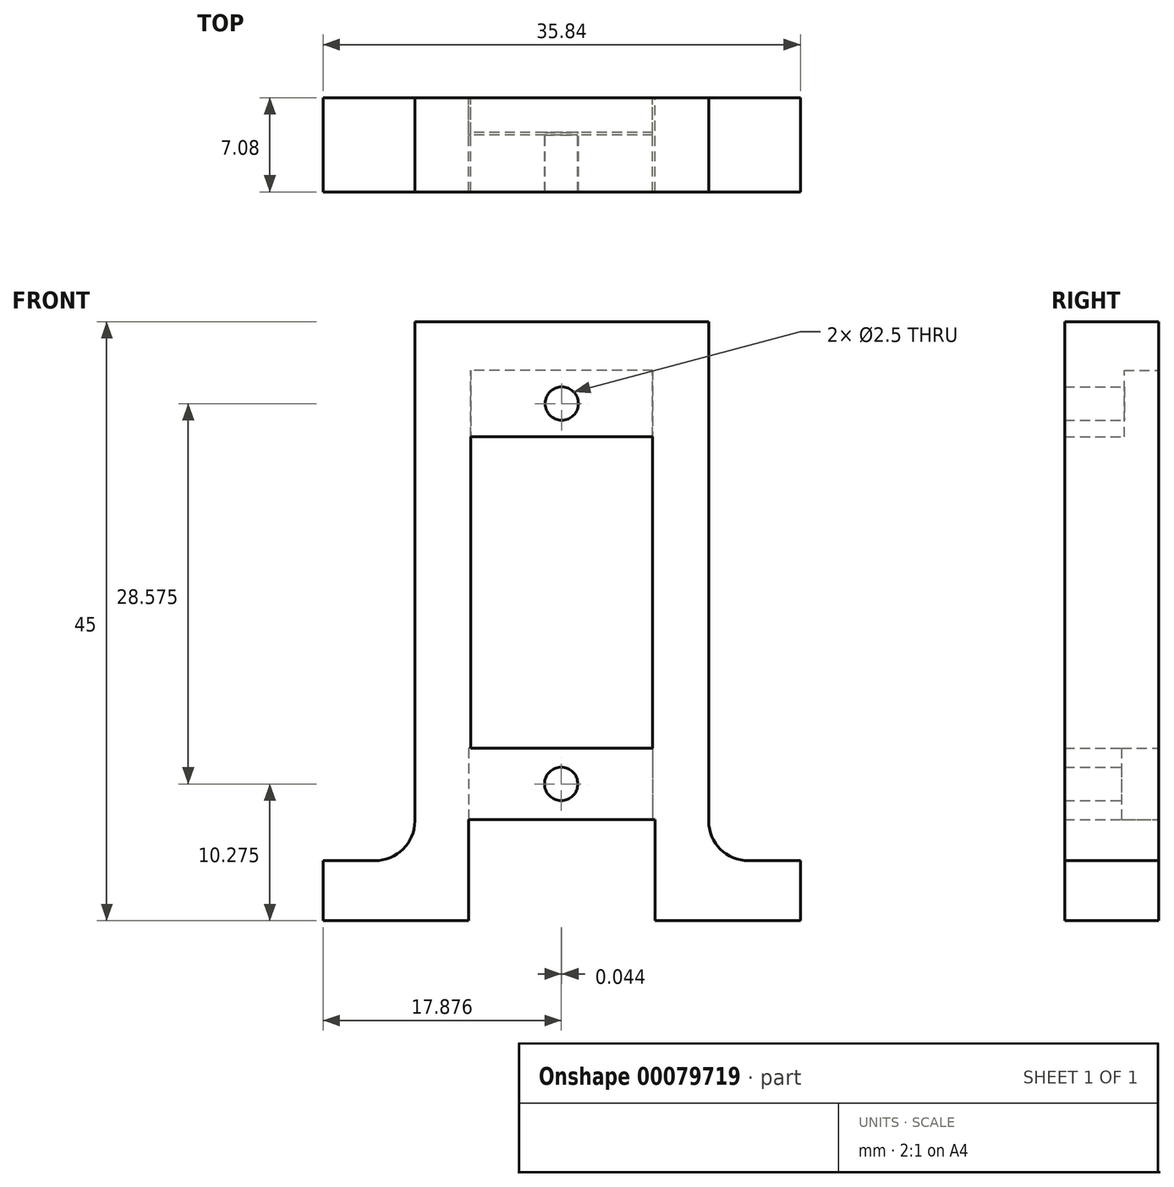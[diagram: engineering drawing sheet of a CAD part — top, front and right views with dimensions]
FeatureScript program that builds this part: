
annotation { "Feature Type Name" : "Feature", "Feature Type Description" : "" }
export const myFeature = defineFeature(function(context is Context, id is Id, definition is map)
    precondition{}
    {
        {
            var Q0;
            Q0=qCreatedBy(makeId("Top.planeOp"),FACE);
            var sketch = newSketch(context, id + "F0", { "sketchPlane" : qUnion([Q0])});
            skLineSegment(sketch, "E0.bottom", {"start": v(17.92, 3.53) * mm, "end": v(-17.92, 3.53) * mm});
            skLineSegment(sketch, "E0.top", {"start": v(17.92, -3.54) * mm, "end": v(-17.92, -3.54) * mm});
            skLineSegment(sketch, "E0.left", {"start": v(17.92, 3.53) * mm, "end": v(17.92, -3.54) * mm});
            skLineSegment(sketch, "E0.right", {"start": v(-17.92, 3.53) * mm, "end": v(-17.92, -3.54) * mm});
            skPoint(sketch, "E0.middle", {"position": v(0, 0) * mm});
            skSolve(sketch);
        }
        {
            var Q0;
            Q0 = qSketchRegion(id + "F0", true);
            extrude(context, id + "F1", {"entities" : qUnion([Q0]), "depth" : 45 * mm});
        }
        {
            var Q0;
            Q0=makeQuery(id+"F1.opExtrude","CAP_FACE",FACE,{"disambiguationData":[OSD([sQuery(id+"F0.wireOp",EDGE,"E0.bottom"),sQuery(id+"F0.wireOp",EDGE,"E0.top"),sQuery(id+"F0.wireOp",EDGE,"E0.left"),sQuery(id+"F0.wireOp",EDGE,"E0.right")])],"isStart":true});
            var sketch = newSketch(context, id + "F2", { "sketchPlane" : qUnion([Q0])});
            skLineSegment(sketch, "E1.bottom", {"start": v(7, 3.54) * mm, "end": v(-7, 3.54) * mm});
            skLineSegment(sketch, "E1.top", {"start": v(7, -3.54) * mm, "end": v(-7, -3.54) * mm});
            skLineSegment(sketch, "E1.left", {"start": v(7, 3.54) * mm, "end": v(7, -3.54) * mm});
            skLineSegment(sketch, "E1.right", {"start": v(-7, 3.54) * mm, "end": v(-7, -3.54) * mm});
            skPoint(sketch, "E1.middle", {"position": v(0, 0) * mm});
            skSolve(sketch);
        }
        {
            var Q0;
            Q0=makeQuery(id+"F1.opExtrude","SWEPT_FACE",FACE,{"disambiguationData":[OSD([sQuery(id+"F0.wireOp",EDGE,"E0.top")])]});
            var sketch = newSketch(context, id + "F3", { "sketchPlane" : qUnion([Q0])});
            skLineSegment(sketch, "E2.bottom", {"start": v(-11.03, 45) * mm, "end": v(11.03, 45) * mm});
            skLineSegment(sketch, "E2.top", {"start": v(-11.03, 0) * mm, "end": v(11.03, 0) * mm});
            skLineSegment(sketch, "E2.left", {"start": v(-11.03, 45) * mm, "end": v(-11.03, 0) * mm});
            skLineSegment(sketch, "E2.right", {"start": v(11.03, 45) * mm, "end": v(11.03, 0) * mm});
            skSolve(sketch);
        }
        {
            var Q0;
            {var subQ0=sQuery(id+"F3.wireOp",EDGE,"E2.right");Q0=makeQuery(id+"F3.imprint","IMPRINT",FACE,{"disambiguationData":[TD([[makeQuery(id+"F3.imprint","IMPRINT",EDGE,{"derivedFrom":subQ0}),1.0]])]});}
            var sketch = newSketch(context, id + "F4", { "sketchPlane" : qUnion([Q0])});
            skLineSegment(sketch, "E3.bottom", {"start": v(11.03, 45) * mm, "end": v(17.92, 45) * mm});
            skLineSegment(sketch, "E3.top", {"start": v(11.03, 4.5) * mm, "end": v(17.92, 4.5) * mm});
            skLineSegment(sketch, "E3.left", {"start": v(11.03, 45) * mm, "end": v(11.03, 4.5) * mm});
            skLineSegment(sketch, "E3.right", {"start": v(17.92, 45) * mm, "end": v(17.92, 4.5) * mm});
            skSolve(sketch);
        }
        {
            var Q0;
            Q0 = qSketchRegion(id + "F4", true);
            var Q1;
            Q1=makeQuery(id+"F1.opExtrude","SWEPT_FACE",FACE,{"disambiguationData":[OSD([sQuery(id+"F0.wireOp",EDGE,"E0.bottom")])]});
            extrude(context, id + "F5", {"entities" : qUnion([Q0]), "operationType" : NewBodyOperationType.REMOVE, "endBound" : BoundingType.UP_TO_SURFACE, "oppositeDirection" : true, "endBoundEntityFace" : qUnion([Q1]), "depth" : 25 * mm});
        }
        {
            var Q0;
            {var subQ0=sQuery(id+"F3.wireOp",EDGE,"E2.left");Q0=makeQuery(id+"F3.imprint","IMPRINT",FACE,{"disambiguationData":[TD([[makeQuery(id+"F3.imprint","IMPRINT",EDGE,{"derivedFrom":subQ0}),-1.0]])]});}
            var sketch = newSketch(context, id + "F6", { "sketchPlane" : qUnion([Q0])});
            skLineSegment(sketch, "E4.bottom", {"start": v(-17.92, 45) * mm, "end": v(-11.03, 45) * mm});
            skLineSegment(sketch, "E4.top", {"start": v(-17.92, 4.5) * mm, "end": v(-11.03, 4.5) * mm});
            skLineSegment(sketch, "E4.left", {"start": v(-17.92, 45) * mm, "end": v(-17.92, 4.5) * mm});
            skLineSegment(sketch, "E4.right", {"start": v(-11.03, 45) * mm, "end": v(-11.03, 4.5) * mm});
            skSolve(sketch);
        }
        {
            var Q0;
            Q0 = qSketchRegion(id + "F6", true);
            var Q1;
            Q1=makeQuery(id+"F1.opExtrude","SWEPT_FACE",FACE,{"disambiguationData":[OSD([sQuery(id+"F0.wireOp",EDGE,"E0.bottom")])]});
            extrude(context, id + "F7", {"entities" : qUnion([Q0]), "operationType" : NewBodyOperationType.REMOVE, "endBound" : BoundingType.UP_TO_SURFACE, "oppositeDirection" : true, "endBoundEntityFace" : qUnion([Q1]), "depth" : 25 * mm});
        }
        {
            var Q0;
            Q0=makeQuery(id+"F1.opExtrude","SWEPT_FACE",FACE,{"disambiguationData":[OSD([sQuery(id+"F0.wireOp",EDGE,"E0.bottom")])]});
            var sketch = newSketch(context, id + "F8", { "sketchPlane" : qUnion([Q0])});
            skSolve(sketch);
        }
        {
            var Q0;
            Q0=makeQuery(id+"F2.imprint","IMPRINT",FACE,{"disambiguationData":[TD([[makeQuery(id+"F2.imprint","IMPRINT",EDGE,{"derivedFrom":sQuery(id+"F2.wireOp",EDGE,"E1.bottom")}),1.0]])]});
            extrude(context, id + "F9", {"entities" : qUnion([Q0]), "operationType" : NewBodyOperationType.REMOVE, "oppositeDirection" : true, "depth" : 7.6 * mm});
        }
        {
            var Q0;
            {var subQ0=sQuery(id+"F0.wireOp",EDGE,"E0.bottom");Q0=makeQuery(id+"F8.imprint","IMPRINT",FACE,{"disambiguationData":[TD([[makeQuery(id+"F8.imprint","IMPRINT",EDGE,{"derivedFrom":makeQuery(id+"F1.opExtrude","CAP_EDGE",EDGE,{"disambiguationData":[OSD([subQ0])],"isStart":true})}),1.0]])]});}
            var sketch = newSketch(context, id + "F10", { "sketchPlane" : qUnion([Q0])});
            skLineSegment(sketch, "E5.bottom", {"start": v(-6.82, 36.35) * mm, "end": v(6.83, 36.35) * mm});
            skLineSegment(sketch, "E5.top", {"start": v(-6.82, 12.95) * mm, "end": v(6.83, 12.95) * mm});
            skLineSegment(sketch, "E5.left", {"start": v(-6.82, 36.35) * mm, "end": v(-6.82, 12.95) * mm});
            skLineSegment(sketch, "E5.right", {"start": v(6.83, 36.35) * mm, "end": v(6.83, 12.95) * mm});
            skSolve(sketch);
        }
        {
            var Q0;
            Q0 = qSketchRegion(id + "F10", true);
            var Q1;
            Q1=makeQuery(id+"F1.opExtrude","SWEPT_FACE",FACE,{"disambiguationData":[OSD([sQuery(id+"F0.wireOp",EDGE,"E0.top")])]});
            extrude(context, id + "F11", {"entities" : qUnion([Q0]), "operationType" : NewBodyOperationType.REMOVE, "endBound" : BoundingType.UP_TO_SURFACE, "oppositeDirection" : true, "endBoundEntityFace" : qUnion([Q1]), "depth" : 25 * mm});
        }
        {
            var Q0;
            Q0=makeQuery(id+"F1.opExtrude","SWEPT_FACE",FACE,{"disambiguationData":[OSD([sQuery(id+"F0.wireOp",EDGE,"E0.bottom")])]});
            var sketch = newSketch(context, id + "F12", { "sketchPlane" : qUnion([Q0])});
            skLineSegment(sketch, "E6.bottom", {"start": v(-6.82, 36.35) * mm, "end": v(6.83, 36.35) * mm});
            skLineSegment(sketch, "E6.top", {"start": v(-6.82, 41.35) * mm, "end": v(6.83, 41.35) * mm});
            skLineSegment(sketch, "E6.left", {"start": v(-6.82, 36.35) * mm, "end": v(-6.82, 41.35) * mm});
            skLineSegment(sketch, "E6.right", {"start": v(6.83, 36.35) * mm, "end": v(6.83, 41.35) * mm});
            skLineSegment(sketch, "E7.bottom", {"start": v(6.83, 36.35) * mm, "end": v(6.83, 36.35) * mm});
            skLineSegment(sketch, "E7.top", {"start": v(6.83, 36.35) * mm, "end": v(6.83, 36.35) * mm});
            skLineSegment(sketch, "E7.left", {"start": v(6.83, 36.35) * mm, "end": v(6.83, 36.35) * mm});
            skLineSegment(sketch, "E7.right", {"start": v(6.83, 36.35) * mm, "end": v(6.83, 36.35) * mm});
            skSolve(sketch);
        }
        {
            var Q0;
            Q0 = qSketchRegion(id + "F12", true);
            extrude(context, id + "F13", {"entities" : qUnion([Q0]), "operationType" : NewBodyOperationType.REMOVE, "oppositeDirection" : true, "depth" : 2.6 * mm});
        }
        {
            var Q0;
            Q0=makeQuery(id+"F1.opExtrude","SWEPT_FACE",FACE,{"disambiguationData":[OSD([sQuery(id+"F0.wireOp",EDGE,"E0.bottom")])]});
            var sketch = newSketch(context, id + "F14", { "sketchPlane" : qUnion([Q0])});
            skLineSegment(sketch, "E8.bottom", {"start": v(-6.82, 12.95) * mm, "end": v(7, 12.95) * mm});
            skLineSegment(sketch, "E8.top", {"start": v(-6.82, 7.6) * mm, "end": v(7, 7.6) * mm});
            skLineSegment(sketch, "E8.left", {"start": v(-6.82, 12.95) * mm, "end": v(-6.82, 7.6) * mm});
            skLineSegment(sketch, "E8.right", {"start": v(7, 12.95) * mm, "end": v(7, 7.6) * mm});
            skSolve(sketch);
        }
        {
            var Q0;
            Q0 = qSketchRegion(id + "F14", true);
            extrude(context, id + "F15", {"entities" : qUnion([Q0]), "operationType" : NewBodyOperationType.REMOVE, "oppositeDirection" : true, "depth" : 2.8 * mm});
        }
        {
            var Q0;
            Q0=makeQuery(id+"F7.boolean.opBoolean","COPY",EDGE,{"derivedFrom":makeQuery(id+"F7.opExtrude","SWEPT_EDGE",EDGE,{"disambiguationData":[OSD([sQuery(id+"F3.wireOp",EDGE,"E2.left"),sQuery(id+"F6.wireOp",EDGE,"E4.top"),sQuery(id+"F6.wireOp",EDGE,"E4.right")])]})});
            var Q1;
            Q1=makeQuery(id+"F5.boolean.opBoolean","COPY",EDGE,{"derivedFrom":makeQuery(id+"F5.opExtrude","SWEPT_EDGE",EDGE,{"disambiguationData":[OSD([sQuery(id+"F3.wireOp",EDGE,"E2.right"),sQuery(id+"F4.wireOp",EDGE,"E3.top"),sQuery(id+"F4.wireOp",EDGE,"E3.left")])]})});
            fillet(context, id + "F16", {"entities" : qUnion([Q0, Q1]), "radius" : 3 * mm, "tangentPropagation" : true, "allowEdgeOverflow" : false});
        }
        {
            var Q0;
            Q0=makeQuery(id+"F15.boolean.opBoolean","COPY",FACE,{"derivedFrom":makeQuery(id+"F15.opExtrude","CAP_FACE",FACE,{"disambiguationData":[OSD([sQuery(id+"F14.wireOp",EDGE,"E8.bottom"),sQuery(id+"F14.wireOp",EDGE,"E8.top"),sQuery(id+"F14.wireOp",EDGE,"E8.left"),sQuery(id+"F14.wireOp",EDGE,"E8.right")])],"isStart":false})});
            var sketch = newSketch(context, id + "F17", { "sketchPlane" : qUnion([Q0])});
            skLineSegment(sketch, "E9", {"start": v(-6.82, 10.27) * mm, "end": v(7, 10.27) * mm, "construction": true});
            skLineSegment(sketch, "E10", {"start": v(0, 12.95) * mm, "end": v(0.09, 7.6) * mm, "construction": true});
            skCircle(sketch, "E11", {"center": v(0.04, 10.27) * mm, "radius": 1.25 * mm});
            skSolve(sketch);
        }
        {
            var Q0;
            Q0 = qSketchRegion(id + "F17", true);
            var Q1;
            Q1=makeQuery(id+"F1.opExtrude","SWEPT_FACE",FACE,{"disambiguationData":[OSD([sQuery(id+"F0.wireOp",EDGE,"E0.top")])]});
            extrude(context, id + "F18", {"entities" : qUnion([Q0]), "operationType" : NewBodyOperationType.REMOVE, "endBound" : BoundingType.UP_TO_SURFACE, "oppositeDirection" : true, "endBoundEntityFace" : qUnion([Q1]), "depth" : 25 * mm});
        }
        {
            var Q0;
            Q0=makeQuery(id+"F13.boolean.opBoolean","COPY",FACE,{"derivedFrom":makeQuery(id+"F13.opExtrude","CAP_FACE",FACE,{"disambiguationData":[OSD([sQuery(id+"F12.wireOp",EDGE,"E6.bottom"),sQuery(id+"F12.wireOp",EDGE,"E6.top"),sQuery(id+"F12.wireOp",EDGE,"E6.left"),sQuery(id+"F12.wireOp",EDGE,"E6.right")])],"isStart":false})});
            var sketch = newSketch(context, id + "F19", { "sketchPlane" : qUnion([Q0])});
            skLineSegment(sketch, "E12", {"start": v(-6.82, 38.85) * mm, "end": v(6.83, 38.85) * mm, "construction": true});
            skLineSegment(sketch, "E13", {"start": v(0, 41.35) * mm, "end": v(0, 36.35) * mm, "construction": true});
            skCircle(sketch, "E14", {"center": v(0, 38.85) * mm, "radius": 1.25 * mm});
            skSolve(sketch);
        }
        {
            var Q0;
            Q0 = qSketchRegion(id + "F19", true);
            var Q1;
            Q1=makeQuery(id+"F1.opExtrude","SWEPT_FACE",FACE,{"disambiguationData":[OSD([sQuery(id+"F0.wireOp",EDGE,"E0.top")])]});
            extrude(context, id + "F20", {"entities" : qUnion([Q0]), "operationType" : NewBodyOperationType.REMOVE, "endBound" : BoundingType.UP_TO_SURFACE, "oppositeDirection" : true, "endBoundEntityFace" : qUnion([Q1]), "depth" : 25 * mm});
        }
    });
